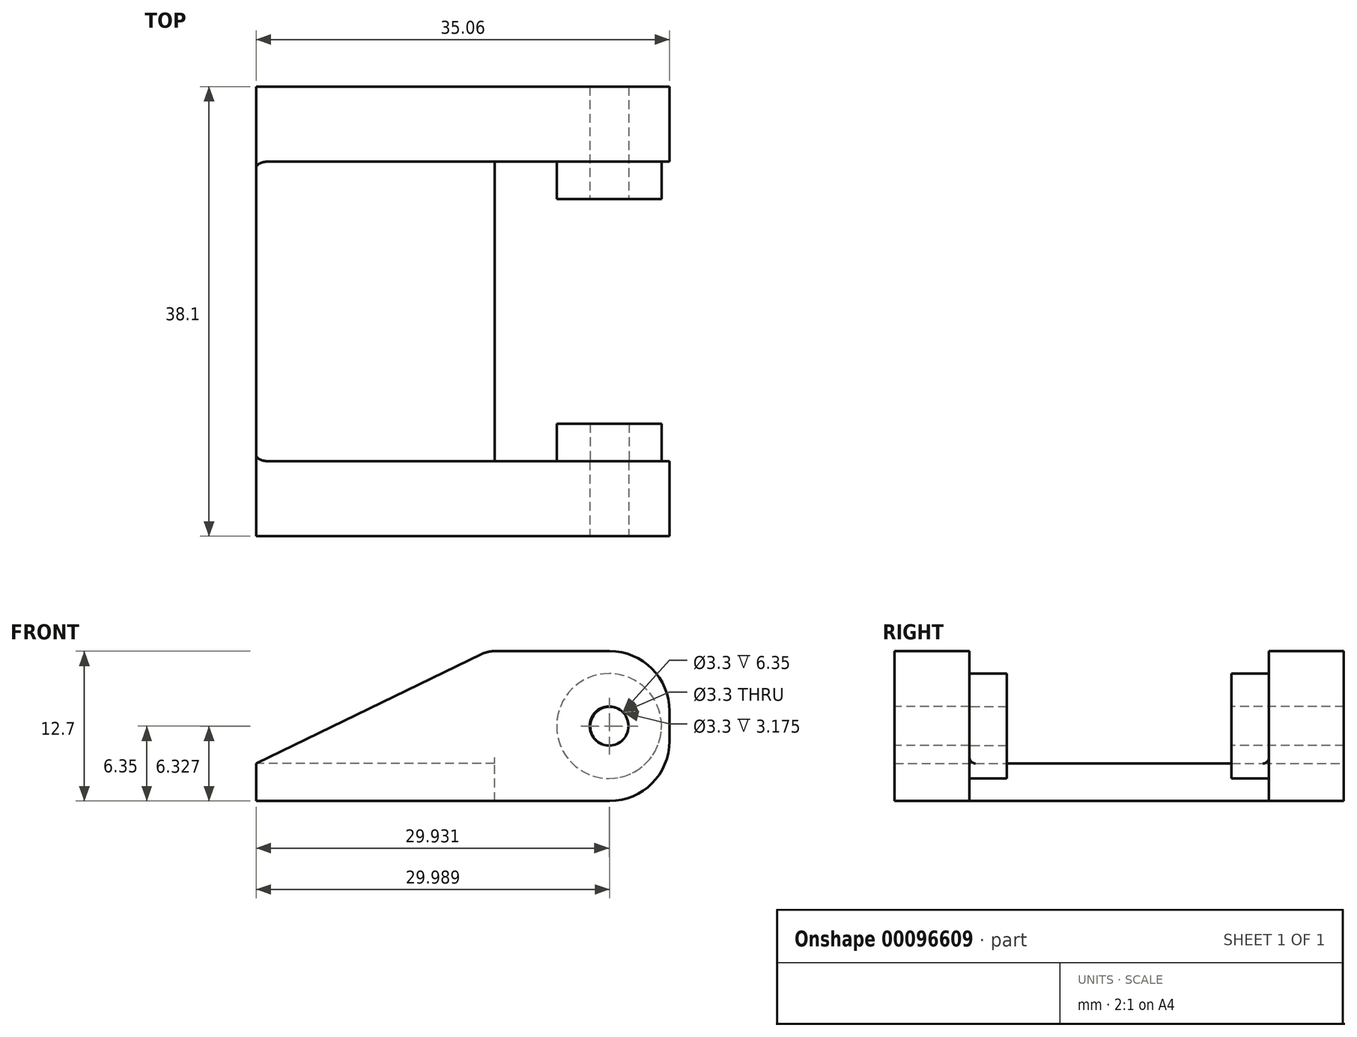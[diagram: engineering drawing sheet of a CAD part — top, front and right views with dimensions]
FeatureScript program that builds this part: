
annotation { "Feature Type Name" : "Feature", "Feature Type Description" : "" }
export const myFeature = defineFeature(function(context is Context, id is Id, definition is map)
    precondition{}
    {
        {
            var Q0;
            Q0=qCreatedBy(makeId("Top.planeOp"),FACE);
            var sketch = newSketch(context, id + "F0", { "sketchPlane" : qUnion([Q0])});
            skLineSegment(sketch, "E0.bottom", {"start": v(9.53, -19.05) * mm, "end": v(-9.52, -19.05) * mm});
            skLineSegment(sketch, "E0.top", {"start": v(9.52, 19.05) * mm, "end": v(-9.53, 19.05) * mm});
            skLineSegment(sketch, "E0.left", {"start": v(9.53, -19.05) * mm, "end": v(9.52, 19.05) * mm});
            skLineSegment(sketch, "E0.right", {"start": v(-9.53, -19.05) * mm, "end": v(-9.53, 19.05) * mm});
            skPoint(sketch, "E0.middle", {"position": v(0, 0) * mm});
            skSolve(sketch);
        }
        {
            var Q0;
            Q0 = qSketchRegion(id + "F0", true);
            extrude(context, id + "F1", {"entities" : qUnion([Q0]), "depth" : 3.17 * mm});
        }
        {
            var Q0;
            Q0=makeQuery(id+"F1.opExtrude","SWEPT_FACE",FACE,{"disambiguationData":[OSD([sQuery(id+"F0.wireOp",EDGE,"E0.bottom")])]});
            var sketch = newSketch(context, id + "F2", { "sketchPlane" : qUnion([Q0])});
            skLineSegment(sketch, "E1.bottom", {"start": v(25.53, 12.7) * mm, "end": v(10.7, 12.7) * mm});
            skLineSegment(sketch, "E1.top", {"start": v(25.53, 0) * mm, "end": v(14.35, 0) * mm});
            skLineSegment(sketch, "E1.left", {"start": v(25.53, 12.7) * mm, "end": v(25.53, 0) * mm});
            skPoint(sketch, "E1.middle", {"position": v(16, 6.35) * mm});
            skCircle(sketch, "E2", {"center": v(20.4, 6.35) * mm, "radius": 1.65 * mm});
            skLineSegment(sketch, "E3", {"start": v(-9.53, 3.18) * mm, "end": v(9.6, 12.45) * mm});
            skPoint(sketch, "E4.newPointA", {"position": v(6.48, 0) * mm});
            skPoint(sketch, "E4.newPointB", {"position": v(20.23, 14.7) * mm});
            skPoint(sketch, "E5.newPointB", {"position": v(6.48, 12.7) * mm});
            skArc(sketch, "E5.filletArc", {"start": v(10.7, 12.7) * mm, "mid": v(10.13, 12.64) * mm, "end": v(9.6, 12.45) * mm});
            skLineSegment(sketch, "E6", {"start": v(14.35, 0) * mm, "end": v(-9.53, 0) * mm});
            skLineSegment(sketch, "E7", {"start": v(-9.53, 0) * mm, "end": v(-9.53, 3.18) * mm});
            skSolve(sketch);
        }
        {
            var Q0;
            Q0=makeQuery(id+"F2.imprint","IMPRINT",FACE,{"disambiguationData":[TD([[makeQuery(id+"F2.imprint","IMPRINT",EDGE,{"derivedFrom":sQuery(id+"F2.wireOp",EDGE,"E1.bottom")}),1.0]])]});
            var Q1;
            Q1=makeQuery(id+"F1.opExtrude","SWEPT_FACE",FACE,{"disambiguationData":[OSD([sQuery(id+"F0.wireOp",EDGE,"E0.top")])]});
            extrude(context, id + "F3", {"entities" : qUnion([Q0]), "operationType" : NewBodyOperationType.ADD, "endBound" : BoundingType.UP_TO_SURFACE, "oppositeDirection" : true, "endBoundEntityFace" : qUnion([Q1]), "depth" : 25.4 * mm});
        }
        {
            var Q0;
            Q0=makeQuery(id+"F3.opExtrude","SWEPT_FACE",FACE,{"disambiguationData":[OSD([sQuery(id+"F2.wireOp",EDGE,"E1.bottom")])]});
            var sketch = newSketch(context, id + "F4", { "sketchPlane" : qUnion([Q0])});
            skLineSegment(sketch, "E8.bottom", {"start": v(35.44, -12.7) * mm, "end": v(-35.44, -12.7) * mm});
            skLineSegment(sketch, "E8.top", {"start": v(35.44, 12.7) * mm, "end": v(-35.44, 12.7) * mm});
            skLineSegment(sketch, "E8.left", {"start": v(35.44, -12.7) * mm, "end": v(35.44, 12.7) * mm});
            skLineSegment(sketch, "E8.right", {"start": v(-35.44, -12.7) * mm, "end": v(-35.44, 12.7) * mm});
            skPoint(sketch, "E8.middle", {"position": v(0, 0) * mm});
            skLineSegment(sketch, "E9", {"start": v(0, 12.7) * mm, "end": v(0, -12.7) * mm});
            skLineSegment(sketch, "E10", {"start": v(0, -12.7) * mm, "end": v(0, 12.7) * mm});
            skSolve(sketch);
        }
        {
            var Q0;
            {var subQ0=sQuery(id+"F4.wireOp",EDGE,"E10");Q0=makeQuery(id+"F4.imprint","IMPRINT",FACE,{"disambiguationData":[TD([[makeQuery(id+"F4.imprint","IMPRINT",EDGE,{"derivedFrom":subQ0}),-1.0]])]});}
            var Q1;
            {var subQ0=sQuery(id+"F4.wireOp",EDGE,"E8.bottom");var subQ1=sQuery(id+"F2.wireOp",EDGE,"E1.bottom");var subQ2=makeQuery(id+"F3.opExtrude","SWEPT_EDGE",EDGE,{"disambiguationData":[OSD([subQ1,sQuery(id+"F2.wireOp",EDGE,"E1.left")])]});var subQ3=makeQuery(id+"F4.imprint","INTERSECT",VERTEX,{"derivedFrom":[subQ2,subQ0]});Q1=makeQuery(id+"F4.imprint","IMPRINT",FACE,{"disambiguationData":[TD([[makeQuery(id+"F4.imprint","IMPRINT",EDGE,{"disambiguationData":[TD([[subQ3,-1.0]])],"derivedFrom":subQ0}),-1.0]])]});}
            var Q2;
            {var subQ0=sQuery(id+"F4.wireOp",EDGE,"E8.left");Q2=makeQuery(id+"F4.imprint","IMPRINT",FACE,{"disambiguationData":[TD([[makeQuery(id+"F4.imprint","IMPRINT",EDGE,{"derivedFrom":subQ0}),1.0]])]});}
            var Q3;
            Q3=makeQuery(id+"F3.boolean.opBoolean","MERGE",VERTEX,{"derivedFrom":[makeQuery(id+"F1.opExtrude","CAP_VERTEX",VERTEX,{"disambiguationData":[OSD([sQuery(id+"F0.wireOp",EDGE,"E0.top"),sQuery(id+"F0.wireOp",EDGE,"E0.right")])],"isStart":false}),makeQuery(id+"F3.opExtrude","CAP_VERTEX",VERTEX,{"disambiguationData":[OSD([sQuery(id+"F0.wireOp",EDGE,"E0.bottom"),sQuery(id+"F2.wireOp",EDGE,"E3")])],"isStart":false})]});
            extrude(context, id + "F5", {"entities" : qUnion([Q0, Q1, Q2]), "operationType" : NewBodyOperationType.REMOVE, "endBound" : BoundingType.THROUGH_ALL, "oppositeDirection" : true, "endBoundEntityVertex" : qUnion([Q3]), "depth" : 25.4 * mm});
        }
        {
            var Q0;
            {var subQ0=sQuery(id+"F2.wireOp",EDGE,"E1.left");var subQ1=sQuery(id+"F2.wireOp",EDGE,"E1.bottom");var subQ2=sQuery(id+"F0.wireOp",EDGE,"E0.bottom");Q0=makeQuery(id+"F5.boolean.opBoolean","SPLIT",EDGE,{"disambiguationData":[TD([makeQuery(id+"F1.opExtrude","SWEPT_FACE",FACE,{"disambiguationData":[OSD([subQ2])]})])],"derivedFrom":makeQuery(id+"F3.opExtrude","SWEPT_EDGE",EDGE,{"disambiguationData":[OSD([subQ1,subQ0])]})});}
            var Q1;
            {var subQ1=sQuery(id+"F2.wireOp",EDGE,"E1.left");var subQ2=sQuery(id+"F2.wireOp",EDGE,"E1.top");var subQ4=sQuery(id+"F0.wireOp",EDGE,"E0.bottom");Q1=makeQuery(id+"F5.boolean.opBoolean","SPLIT",EDGE,{"disambiguationData":[TD([makeQuery(id+"F1.opExtrude","SWEPT_FACE",FACE,{"disambiguationData":[OSD([subQ4])]})])],"derivedFrom":makeQuery(id+"F3.opExtrude","SWEPT_EDGE",EDGE,{"disambiguationData":[OSD([subQ2,subQ1])]})});}
            var Q2;
            {var subQ1=sQuery(id+"F2.wireOp",EDGE,"E1.left");var subQ2=sQuery(id+"F2.wireOp",EDGE,"E1.top");var subQ5=sQuery(id+"F0.wireOp",EDGE,"E0.top");Q2=makeQuery(id+"F5.boolean.opBoolean","SPLIT",EDGE,{"disambiguationData":[TD([makeQuery(id+"F1.opExtrude","SWEPT_FACE",FACE,{"disambiguationData":[OSD([subQ5])]})])],"derivedFrom":makeQuery(id+"F3.opExtrude","SWEPT_EDGE",EDGE,{"disambiguationData":[OSD([subQ2,subQ1])]})});}
            var Q3;
            {var subQ0=sQuery(id+"F2.wireOp",EDGE,"E1.left");var subQ1=sQuery(id+"F2.wireOp",EDGE,"E1.bottom");Q3=makeQuery(id+"F5.boolean.opBoolean","SPLIT",EDGE,{"disambiguationData":[TD([makeQuery(id+"F1.opExtrude","SWEPT_FACE",FACE,{"disambiguationData":[OSD([sQuery(id+"F0.wireOp",EDGE,"E0.top")])]})])],"derivedFrom":makeQuery(id+"F3.opExtrude","SWEPT_EDGE",EDGE,{"disambiguationData":[OSD([subQ1,subQ0])]})});}
            fillet(context, id + "F6", {"entities" : qUnion([Q0, Q1, Q2, Q3]), "radius" : 5.08 * mm, "tangentPropagation" : true, "allowEdgeOverflow" : false});
        }
        {
            var Q0;
            {var subQ2=sQuery(id+"F2.wireOp",EDGE,"E1.bottom");var subQ3=sQuery(id+"F0.wireOp",EDGE,"E0.bottom");Q0=makeQuery(id+"F5.boolean.opBoolean","SPLIT",FACE,{"disambiguationData":[TD([makeQuery(id+"F1.opExtrude","SWEPT_FACE",FACE,{"disambiguationData":[OSD([subQ3])]})])],"derivedFrom":makeQuery(id+"F3.opExtrude","SWEPT_FACE",FACE,{"disambiguationData":[OSD([subQ2])]})});}
            var sketch = newSketch(context, id + "F7", { "sketchPlane" : qUnion([Q0])});
            skLineSegment(sketch, "E11.bottom", {"start": v(10.7, -12.7) * mm, "end": v(-19.36, -12.7) * mm});
            skLineSegment(sketch, "E11.top", {"start": v(10.7, 12.7) * mm, "end": v(-19.36, 12.7) * mm});
            skLineSegment(sketch, "E11.left", {"start": v(10.7, -12.7) * mm, "end": v(10.7, 12.7) * mm});
            skLineSegment(sketch, "E11.right", {"start": v(-19.36, -12.7) * mm, "end": v(-19.36, 12.7) * mm});
            skSolve(sketch);
        }
        {
            var Q0;
            Q0 = qSketchRegion(id + "F7", true);
            var Q1;
            {var subQ0=sQuery(id+"F0.wireOp",EDGE,"E0.bottom");Q1=makeQuery(id+"F3.boolean.opBoolean","MERGE",VERTEX,{"derivedFrom":[makeQuery(id+"F1.opExtrude","CAP_VERTEX",VERTEX,{"disambiguationData":[OSD([subQ0,sQuery(id+"F0.wireOp",EDGE,"E0.right")])],"isStart":false}),makeQuery(id+"F3.opExtrude","CAP_VERTEX",VERTEX,{"disambiguationData":[OSD([subQ0,sQuery(id+"F2.wireOp",EDGE,"E3"),sQuery(id+"F2.wireOp",EDGE,"E7")])],"isStart":true})]});}
            extrude(context, id + "F8", {"entities" : qUnion([Q0]), "operationType" : NewBodyOperationType.REMOVE, "endBound" : BoundingType.UP_TO_VERTEX, "oppositeDirection" : true, "endBoundEntityVertex" : qUnion([Q1]), "depth" : 25.4 * mm});
        }
        {
            var Q0;
            Q0=makeQuery(id+"F8.boolean.opBoolean","MERGE",FACE,{"derivedFrom":[makeQuery(id+"F5.boolean.opBoolean","COPY",FACE,{"derivedFrom":makeQuery(id+"F5.opExtrude","SWEPT_FACE",FACE,{"disambiguationData":[OSD([sQuery(id+"F4.wireOp",EDGE,"E8.bottom")])]})})],"fromTools":[makeQuery(id+"F8.opExtrude","SWEPT_FACE",FACE,{"disambiguationData":[OSD([sQuery(id+"F7.wireOp",EDGE,"E11.bottom")])]})]});
            var sketch = newSketch(context, id + "F9", { "sketchPlane" : qUnion([Q0])});
            skCircle(sketch, "E12", {"center": v(-20.4, 6.35) * mm, "radius": 4.45 * mm});
            skCircle(sketch, "E13", {"center": v(-20.46, 6.33) * mm, "radius": 1.65 * mm});
            skSolve(sketch);
        }
        {
            var Q0;
            Q0 = qSketchRegion(id + "F9", true);
            extrude(context, id + "F10", {"entities" : qUnion([Q0]), "operationType" : NewBodyOperationType.ADD, "depth" : 3.17 * mm});
        }
        {
            var Q0;
            Q0=makeQuery(id+"F8.boolean.opBoolean","MERGE",FACE,{"derivedFrom":[makeQuery(id+"F5.boolean.opBoolean","COPY",FACE,{"derivedFrom":makeQuery(id+"F5.opExtrude","SWEPT_FACE",FACE,{"disambiguationData":[OSD([sQuery(id+"F4.wireOp",EDGE,"E8.top")])]})})],"fromTools":[makeQuery(id+"F8.opExtrude","SWEPT_FACE",FACE,{"disambiguationData":[OSD([sQuery(id+"F7.wireOp",EDGE,"E11.top")])]})]});
            var sketch = newSketch(context, id + "F11", { "sketchPlane" : qUnion([Q0])});
            skCircle(sketch, "E14", {"center": v(20.4, 6.35) * mm, "radius": 4.45 * mm});
            skCircle(sketch, "E15", {"center": v(20.4, 6.35) * mm, "radius": 1.65 * mm});
            skSolve(sketch);
        }
        {
            var Q0;
            Q0 = qSketchRegion(id + "F11", true);
            extrude(context, id + "F12", {"entities" : qUnion([Q0]), "operationType" : NewBodyOperationType.ADD, "depth" : 3.17 * mm});
        }
        {
            var Q0;
            Q0=makeQuery(id+"F3.boolean.opBoolean","MERGE",FACE,{"derivedFrom":[makeQuery(id+"F1.opExtrude","CAP_FACE",FACE,{"disambiguationData":[OSD([sQuery(id+"F0.wireOp",EDGE,"E0.bottom"),sQuery(id+"F0.wireOp",EDGE,"E0.top"),sQuery(id+"F0.wireOp",EDGE,"E0.left"),sQuery(id+"F0.wireOp",EDGE,"E0.right")])],"isStart":true}),makeQuery(id+"F3.opExtrude","SWEPT_FACE",FACE,{"disambiguationData":[OSD([sQuery(id+"F2.wireOp",EDGE,"E1.top"),sQuery(id+"F2.wireOp",EDGE,"E6")])]})]});
            var sketch = newSketch(context, id + "F13", { "sketchPlane" : qUnion([Q0])});
            skLineSegment(sketch, "E16.bottom", {"start": v(0, 12.7) * mm, "end": v(5.08, 12.7) * mm});
            skLineSegment(sketch, "E16.top", {"start": v(0, -12.7) * mm, "end": v(5.08, -12.7) * mm});
            skLineSegment(sketch, "E16.left", {"start": v(0, 12.7) * mm, "end": v(0, -12.7) * mm});
            skLineSegment(sketch, "E16.right", {"start": v(5.08, 12.7) * mm, "end": v(5.08, -12.7) * mm});
            skSolve(sketch);
        }
        {
            var Q0;
            Q0 = qSketchRegion(id + "F13", true);
            var Q1;
            Q1=makeQuery(id+"F8.boolean.opBoolean","COPY",FACE,{"derivedFrom":makeQuery(id+"F8.opExtrude","CAP_FACE",FACE,{"disambiguationData":[OSD([sQuery(id+"F7.wireOp",EDGE,"E11.bottom"),sQuery(id+"F7.wireOp",EDGE,"E11.top"),sQuery(id+"F7.wireOp",EDGE,"E11.left"),sQuery(id+"F7.wireOp",EDGE,"E11.right")])],"isStart":false})});
            extrude(context, id + "F14", {"entities" : qUnion([Q0]), "operationType" : NewBodyOperationType.ADD, "endBound" : BoundingType.UP_TO_SURFACE, "oppositeDirection" : true, "endBoundEntityFace" : qUnion([Q1]), "depth" : 25.4 * mm});
        }
        {
            var Q0;
            Q0=makeQuery(id+"F14.boolean.opBoolean","MERGE",EDGE,{"derivedFrom":[makeQuery(id+"F8.boolean.opBoolean","COPY",EDGE,{"derivedFrom":makeQuery(id+"F8.opExtrude","CAP_EDGE",EDGE,{"disambiguationData":[OSD([sQuery(id+"F7.wireOp",EDGE,"E11.bottom")])],"isStart":false})}),makeQuery(id+"F14.opExtrude","CAP_EDGE",EDGE,{"disambiguationData":[OSD([sQuery(id+"F13.wireOp",EDGE,"E16.bottom")])],"isStart":false})]});
            var Q1;
            Q1=makeQuery(id+"F14.boolean.opBoolean","MERGE",EDGE,{"derivedFrom":[makeQuery(id+"F8.boolean.opBoolean","COPY",EDGE,{"derivedFrom":makeQuery(id+"F8.opExtrude","CAP_EDGE",EDGE,{"disambiguationData":[OSD([sQuery(id+"F7.wireOp",EDGE,"E11.top")])],"isStart":false})}),makeQuery(id+"F14.opExtrude","CAP_EDGE",EDGE,{"disambiguationData":[OSD([sQuery(id+"F13.wireOp",EDGE,"E16.top")])],"isStart":false})]});
            fillet(context, id + "F15", {"entities" : qUnion([Q0, Q1]), "radius" : 0.5 * mm, "tangentPropagation" : true, "allowEdgeOverflow" : false});
        }
    });
